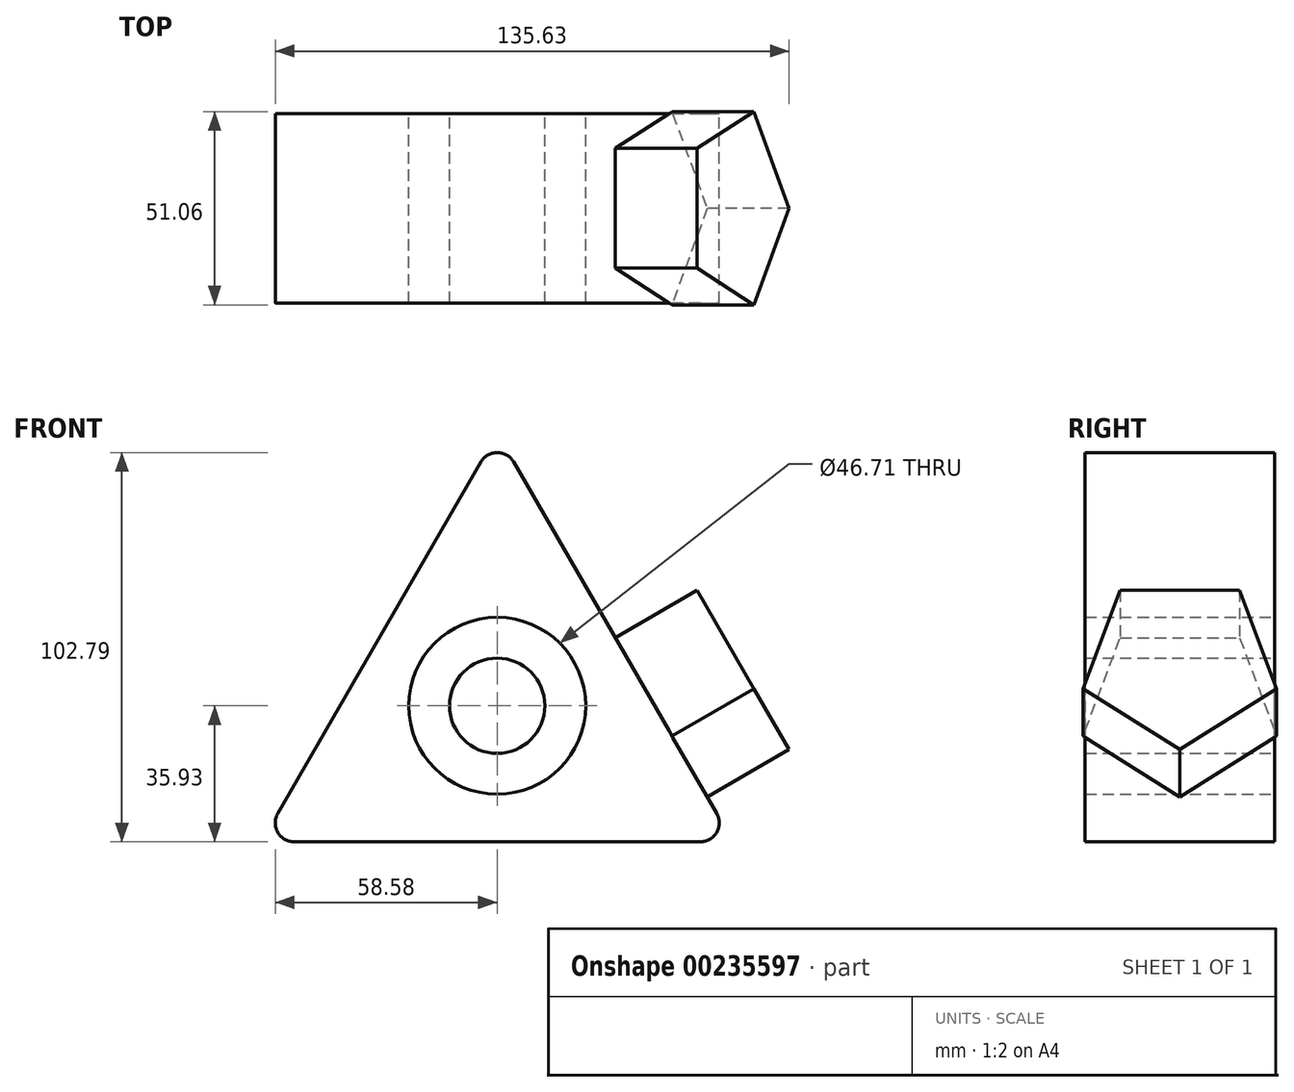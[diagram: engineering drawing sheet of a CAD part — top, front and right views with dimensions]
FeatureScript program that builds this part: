
annotation { "Feature Type Name" : "Feature", "Feature Type Description" : "" }
export const myFeature = defineFeature(function(context is Context, id is Id, definition is map)
    precondition{}
    {
        {
            var Q0;
            Q0=qCreatedBy(makeId("Front.planeOp"),FACE);
            var sketch = newSketch(context, id + "F0", { "sketchPlane" : qUnion([Q0])});
            skCircle(sketch, "E0.cCircle", {"center": v(0, 0) * mm, "radius": 35.93 * mm, "construction": true});
            skLineSegment(sketch, "E0.0", {"start": v(62.24, -35.93) * mm, "end": v(-62.24, -35.93) * mm});
            skLineSegment(sketch, "E0.1", {"start": v(-62.24, -35.93) * mm, "end": v(0, 71.86) * mm});
            skLineSegment(sketch, "E0.2", {"start": v(0, 71.86) * mm, "end": v(62.24, -35.93) * mm});
            skPoint(sketch, "E0.0.midPoint", {"position": v(0, -35.93) * mm});
            skCircle(sketch, "E1", {"center": v(0, 0) * mm, "radius": 23.36 * mm});
            skCircle(sketch, "E2", {"center": v(0, 0) * mm, "radius": 12.6 * mm});
            skSolve(sketch);
        }
        {
            var Q0;
            Q0 = qSketchRegion(id + "F0", true);
            var Q1;
            Q1=makeQuery(id+"F0.imprint","IMPRINT",FACE,{"disambiguationData":[TD([[makeQuery(id+"F0.imprint","IMPRINT",EDGE,{"derivedFrom":sQuery(id+"F0.wireOp",EDGE,"E2")}),1.0]])]});
            extrude(context, id + "F1", {"entities" : qUnion([Q0, Q1]), "depth" : 25 * mm, "hasSecondDirection" : true, "secondDirectionOppositeDirection" : true, "secondDirectionDepth" : 25 * mm});
        }
        {
            var Q0;
            Q0=makeQuery(id+"F1.opExtrude","SWEPT_FACE",FACE,{"disambiguationData":[OSD([sQuery(id+"F0.wireOp",EDGE,"E0.2")])]});
            var sketch = newSketch(context, id + "F2", { "sketchPlane" : qUnion([Q0])});
            skCircle(sketch, "E3.cCircle", {"center": v(0, -21.71) * mm, "radius": 21.71 * mm, "construction": true});
            skLineSegment(sketch, "E3.0", {"start": v(-15.78, 0) * mm, "end": v(15.78, 0) * mm});
            skLineSegment(sketch, "E3.1", {"start": v(15.78, 0) * mm, "end": v(25.53, -30) * mm});
            skLineSegment(sketch, "E3.2", {"start": v(25.53, -30) * mm, "end": v(0, -48.55) * mm});
            skLineSegment(sketch, "E3.3", {"start": v(0, -48.55) * mm, "end": v(-25.53, -30) * mm});
            skLineSegment(sketch, "E3.4", {"start": v(-25.53, -30) * mm, "end": v(-15.78, 0) * mm});
            skPoint(sketch, "E3.0.midPoint", {"position": v(0, 0) * mm});
            skSolve(sketch);
        }
        {
            var Q0;
            {var subQ0=sQuery(id+"F2.wireOp",EDGE,"E3.2");var subQ1=sQuery(id+"F2.wireOp",EDGE,"E3.1");var subQ2=makeQuery(id+"F2.imprint","INTERSECT",VERTEX,{"derivedFrom":[subQ1,subQ0]});Q0=makeQuery(id+"F2.imprint","IMPRINT",FACE,{"disambiguationData":[TD([[makeQuery(id+"F2.imprint","IMPRINT",EDGE,{"disambiguationData":[TD([[subQ2,1.0]])],"derivedFrom":subQ1}),-1.0]])]});}
            var Q1;
            {var subQ0=sQuery(id+"F2.wireOp",EDGE,"E3.4");var subQ1=sQuery(id+"F2.wireOp",EDGE,"E3.3");var subQ2=makeQuery(id+"F2.imprint","INTERSECT",VERTEX,{"derivedFrom":[subQ1,subQ0]});Q1=makeQuery(id+"F2.imprint","IMPRINT",FACE,{"disambiguationData":[TD([[makeQuery(id+"F2.imprint","IMPRINT",EDGE,{"disambiguationData":[TD([[subQ2,1.0]])],"derivedFrom":subQ1}),-1.0]])]});}
            var Q2;
            {var subQ11=sQuery(id+"F2.wireOp",EDGE,"E3.0");Q2=makeQuery(id+"F2.imprint","IMPRINT",FACE,{"disambiguationData":[TD([[makeQuery(id+"F2.imprint","IMPRINT",EDGE,{"derivedFrom":subQ11}),-1.0]])]});}
            extrude(context, id + "F3", {"entities" : qUnion([Q0, Q1, Q2]), "operationType" : NewBodyOperationType.ADD, "depth" : 25 * mm});
        }
        {
            var Q0;
            Q0=makeQuery(id+"F1.opExtrude","SWEPT_EDGE",EDGE,{"disambiguationData":[OSD([sQuery(id+"F0.wireOp",EDGE,"E0.1"),sQuery(id+"F0.wireOp",EDGE,"E0.2")])]});
            fillet(context, id + "F4", {"entities" : qUnion([Q0]), "radius" : 5 * mm, "tangentPropagation" : true, "allowEdgeOverflow" : false});
        }
        {
            var Q0;
            Q0=makeQuery(id+"F1.opExtrude","SWEPT_EDGE",EDGE,{"disambiguationData":[OSD([sQuery(id+"F0.wireOp",EDGE,"E0.0"),sQuery(id+"F0.wireOp",EDGE,"E0.2")])]});
            fillet(context, id + "F5", {"entities" : qUnion([Q0]), "radius" : 5 * mm, "tangentPropagation" : true, "allowEdgeOverflow" : false});
        }
        {
            var Q0;
            Q0=makeQuery(id+"F1.opExtrude","SWEPT_EDGE",EDGE,{"disambiguationData":[OSD([sQuery(id+"F0.wireOp",EDGE,"E0.0"),sQuery(id+"F0.wireOp",EDGE,"E0.1")])]});
            fillet(context, id + "F6", {"entities" : qUnion([Q0]), "radius" : 5 * mm, "tangentPropagation" : true, "allowEdgeOverflow" : false});
        }
    });
